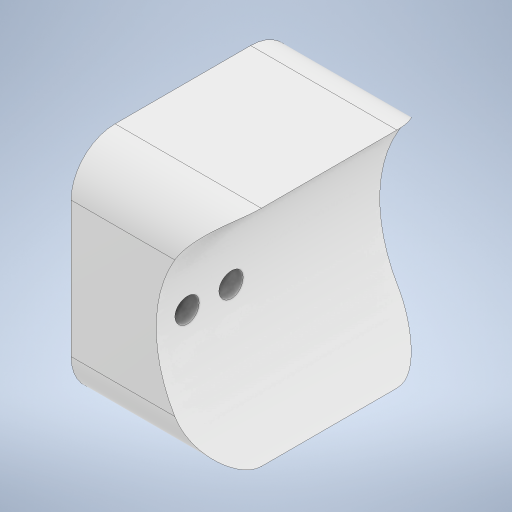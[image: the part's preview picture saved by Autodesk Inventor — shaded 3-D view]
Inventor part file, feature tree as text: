
AUTODESK INVENTOR PART (.ipt)
format: ipt  version: 2023 (Build 270158030, 158C)  size: 242,688 bytes
history: native  units: in
note: dims shown in document units (in); Inventor stores cm internally (conversion verified against a paired STEP export)
features: extrude x2, sketch x2, fillet x1
ambient origin geometry x8: Origin, YZ Plane, XZ Plane, XY Plane, X Axis, Y Axis, Z Axis, Center Point
bodies: Solid1 (feature_tree)
feature tree (5):
  extrude  "Extrusion1"  Depth=1.9488in
  extrude  "Extrusion2"  Depth=0.3937in TaperAngle=0.0deg
  fillet  "Fillet1"  [1 undecoded]
  sketch  "Sketch1"  dims[d0=2.375in d1=1.9488in]
  sketch  "Sketch2"  dims[d2=2.0in d3=2.0in d4=0.0in d6=0.0in d7=0.0in d8=0.2165in d9=0.2756in d10=0.3937in d11=0.3937in]
note: 1 required parameter value undecoded (feature->parameter linkage not recoverable at this tier; creation-order binding heuristic only, values carry confidence <= 0.55)
